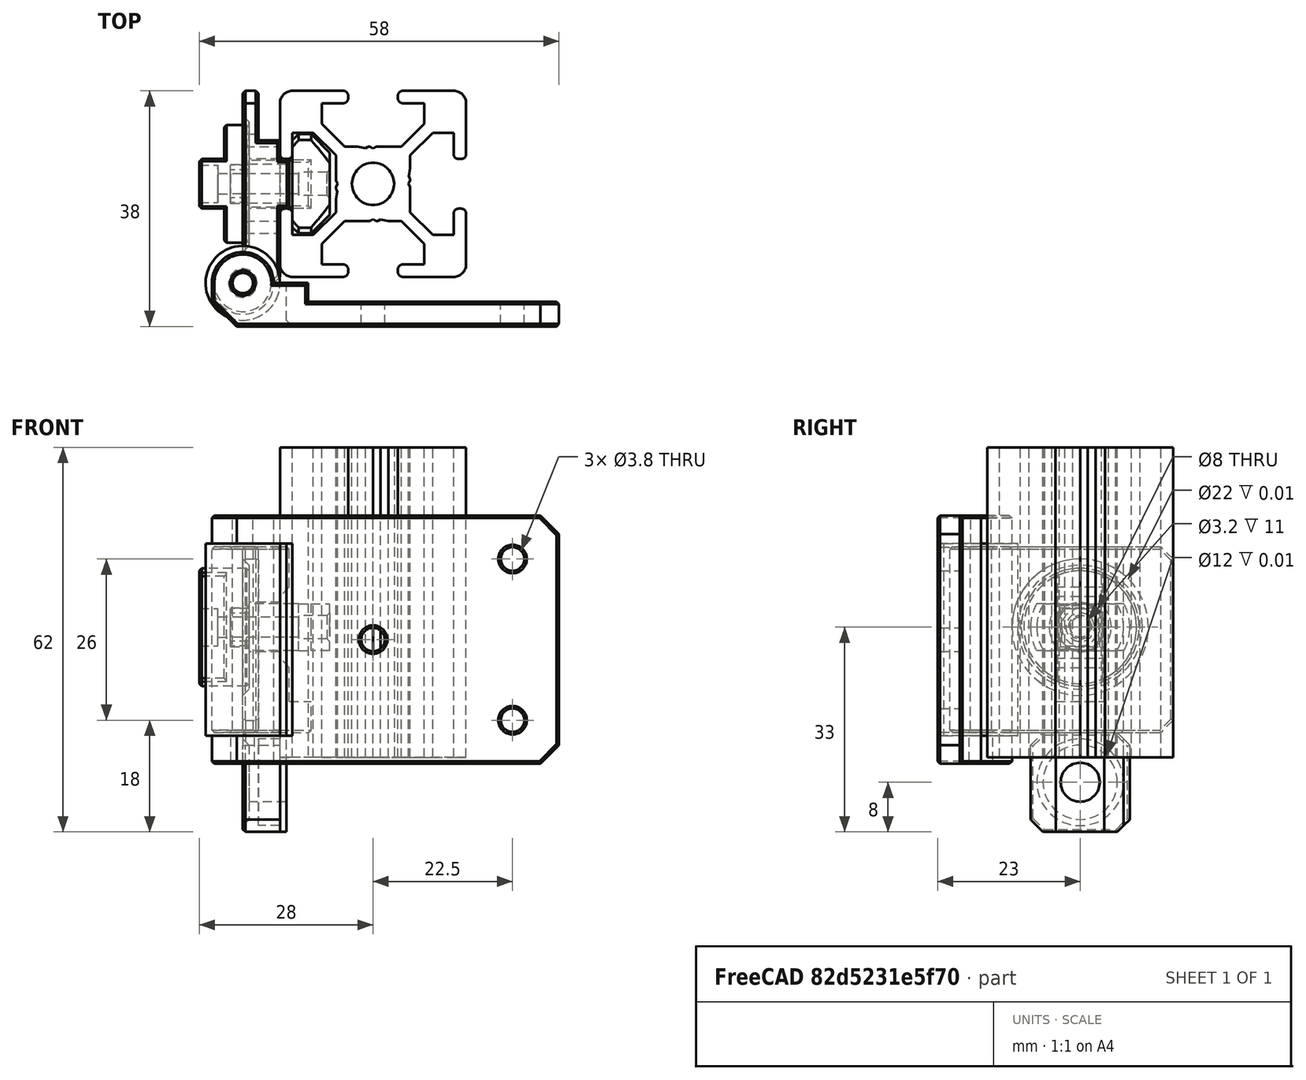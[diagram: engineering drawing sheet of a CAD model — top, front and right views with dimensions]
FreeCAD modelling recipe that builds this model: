
FCSTD DOCUMENT  (FreeCAD 0.19R24291 (Git))
Label: door-quick-release
License: Other
LicenseURL: GPL3
objects: Part::Cylinder×22, Part::Chamfer×18, Part::Box×16, Part::Cut×12, Part::MultiFuse×11, Part::Refine×3, Part::MultiCommon×3, Part::Feature×1, Part::Extrusion×1
note: 87 computed .brp shape members not serialized (recipe doc carries the construction recipe); baked Part::Feature solids carry a one-line shape summary decoded from their .brp

FEATURE [Part::Box] Box019  label="Cube018"
  AttacherType = Attacher::AttachEngine3D
  Height = 30
  Length = 6
  Placement = pos=(-6,0,0) rot=(0,0,1;0rad)
  Width = 30
FEATURE [Part::Box] Box020  label="Cube019"
  AttacherType = Attacher::AttachEngine3D
  Height = 12
  Length = 1.5
  Placement = pos=(0,11.1,0) rot=(0,0,1;0rad)
  Width = 7.8
FEATURE [Part::Cylinder] Cylinder
  Angle = 360
  AttacherType = Attacher::AttachEngine3D
  Height = 10
  Placement = pos=(3,15,17) rot=(0,-1,0;1.5708rad)
  Radius = 4
FEATURE [Part::Cylinder] Cylinder001
  Angle = 360
  AttacherType = Attacher::AttachEngine3D
  Height = 10
  Placement = pos=(-5,15,17) rot=(0,-1,0;1.5708rad)
  Radius = 11
FEATURE [Part::Cylinder] Cylinder002
  Angle = 360
  AttacherType = Attacher::AttachEngine3D
  Height = 30
  Placement = pos=(-6,-1,0) rot=(0,0,1;0rad)
  Radius = 5
FEATURE [Part::Box] Box  label="Cube"
  AttacherType = Attacher::AttachEngine3D
  Height = 30
  Length = 2
  Placement = pos=(-2,-1,0) rot=(0,0,1;0rad)
  Width = 2
FEATURE [Part::Chamfer] Chamfer006006002
  Base = -> Box
  Edges = 1 edges r=1: [Edge5]
FEATURE [Part::Cylinder] Cylinder003
  Angle = 360
  AttacherType = Attacher::AttachEngine3D
  Height = 30
  Placement = pos=(-6,-1,0) rot=(0,0,1;0rad)
  Radius = 1.7
FEATURE [Part::Box] Box021  label="Cube020"
  AttacherType = Attacher::AttachEngine3D
  Height = 5
  Length = 5
  Placement = pos=(0,11.1,0) rot=(0,0,1;0rad)
  Width = 7.8
FEATURE [Part::Box] Box022  label="Cube021"
  AttacherType = Attacher::AttachEngine3D
  Height = 8
  Length = 1.5
  Placement = pos=(0,11.1,22) rot=(0,0,1;0rad)
  Width = 7.8
FEATURE [Part::Chamfer] Chamfer
  Base = -> Box020
  Edges = 1 edges r=1.49: [Edge6]
FEATURE [Part::Chamfer] Chamfer006006003
  Base = -> Box022
  Edges = 1 edges r=1.49: [Edge8]
FEATURE [Part::Chamfer] Chamfer006006004
  Base = -> Box019
  Edges = 2 edges r=2: [Edge11,Edge12]
FEATURE [Part::Cut] Cut
  Base = -> Chamfer006006004
  Tool = -> Cylinder
FEATURE [Part::Cut] Cut001
  Base = -> Cut
  Tool = -> Cylinder001
FEATURE [Part::Chamfer] Chamfer006006005
  Base = -> Cut001
  Edges = 1 edges r=0.99: [Edge21]
FEATURE [Part::MultiFuse] Fusion
  Shapes = -> [Chamfer006006005,Chamfer006006003,Chamfer,Box021,Chamfer006006002,Cylinder002]
FEATURE [Part::Cut] Cut002
  Base = -> Fusion
  Tool = -> Cylinder003
FEATURE [Part::Refine] Cut002001
  Source = -> Cut002
FEATURE [Part::Cylinder] Cylinder004
  Angle = 360
  AttacherType = Attacher::AttachEngine3D
  Height = 40
  Placement = pos=(-6,-1,0) rot=(0,0,1;0rad)
  Radius = 5
FEATURE [Part::Box] Box023  label="Cube022"
  AttacherType = Attacher::AttachEngine3D
  Height = 40
  Length = 46
  Placement = pos=(4.5,-4,0) rot=(0,0,1;0rad)
  Width = 4
FEATURE [Part::Box] Box024  label="Cube023"
  AttacherType = Attacher::AttachEngine3D
  Height = 40
  Length = 56
  Placement = pos=(-11,-8,0) rot=(0,0,1;0rad)
  Width = 7
FEATURE [Part::Cylinder] Cylinder005
  Angle = 360
  AttacherType = Attacher::AttachEngine3D
  Height = 31
  Placement = pos=(-6,-1,4.5) rot=(0,0,1;0rad)
  Radius = 6
FEATURE [Part::Chamfer] Chamfer006006007
  Base = -> Box024
  Edges = 1 edges r=4: [Edge1]
FEATURE [Part::Cut] Cut002002
  Base = -> Chamfer006006007
  Tool = -> Box023
FEATURE [Part::Chamfer] Chamfer006006008
  Base = -> Cut002002
  Edges = 2 edges r=3: [Edge8,Edge16]
FEATURE [Part::MultiFuse] Fusion001
  Shapes = -> [Chamfer006006008,Cylinder004]
FEATURE [Part::Box] Box025  label="Cube024"
  AttacherType = Attacher::AttachEngine3D
  Height = 31
  Length = 13
  Placement = pos=(-12,-9,4.5) rot=(0,0,1;0rad)
  Width = 14
FEATURE [Part::Cut] Cut002003
  Base = -> Fusion001
  Tool = -> Box025
FEATURE [Part::Chamfer] Chamfer006006009
  Base = -> Cut002003
  Edges = 1 edges r=1: [Edge18]
FEATURE [Part::Cylinder] Cylinder006
  Angle = 360
  AttacherType = Attacher::AttachEngine3D
  Height = 10
  Placement = pos=(-6,-1,0) rot=(0,0,1;0rad)
  Radius = 1.9
FEATURE [Part::Cylinder] Cylinder007
  Angle = 360
  AttacherType = Attacher::AttachEngine3D
  Height = 10
  Placement = pos=(15,-9,20) rot=(-1,0,0;1.5708rad)
  Radius = 1.9
FEATURE [Part::Cylinder] Cylinder008
  Angle = 360
  AttacherType = Attacher::AttachEngine3D
  Height = 10
  Placement = pos=(37.5,-9,33) rot=(-1,0,0;1.5708rad)
  Radius = 1.9
FEATURE [Part::Cylinder] Cylinder009
  Angle = 360
  AttacherType = Attacher::AttachEngine3D
  Height = 10
  Placement = pos=(37.5,-9,7) rot=(-1,0,0;1.5708rad)
  Radius = 1.9
FEATURE [Part::MultiFuse] Fusion002
  Shapes = -> [Cylinder009,Cylinder008,Cylinder007]
FEATURE [Part::Cylinder] Cylinder010
  Angle = 360
  AttacherType = Attacher::AttachEngine3D
  Height = 10
  Placement = pos=(-6,-1,30) rot=(0,0,1;0rad)
  Radius = 1.65
FEATURE [Part::MultiFuse] Fusion003
  Shapes = -> [Cylinder010,Cylinder006]
FEATURE [Part::MultiFuse] Fusion004
  Shapes = -> [Fusion003,Fusion002]
FEATURE [Part::Cut] Cut002004
  Base = -> Chamfer006006009
  Tool = -> Fusion004
FEATURE [Part::Refine] Cut002004001
  Source = -> Cut002004
FEATURE [Part::Chamfer] Chamfer006006010
  Base = -> Cut002004001
  Edges = 27 edges r=0.4: [Edge5,Edge6,Edge8,Edge9,Edge10,Edge11,Edge12,Edge13,Edge23,Edge32,Edge34,Edge36,Edge39,Edge47,Edge49,Edge52,Edge54,Edge56,Edge57,Edge59,Edge60,Edge62,Edge63,Edge64,Edge65,Edge67,Edge68]
FEATURE [Part::Box] Box026  label="Cube025"
  AttacherType = Attacher::AttachEngine3D
  Height = 16
  Length = 6
  Placement = pos=(-6,7,0) rot=(0,0,1;0rad)
  Width = 16
FEATURE [Part::Box] Box027  label="Cube026"
  AttacherType = Attacher::AttachEngine3D
  Height = 16
  Length = 1
  Placement = pos=(0,11.1,0) rot=(0,0,1;0rad)
  Width = 7.8
FEATURE [Part::Cylinder] Cylinder011
  Angle = 360
  AttacherType = Attacher::AttachEngine3D
  Height = 10
  Placement = pos=(2,15,8) rot=(0,-1,0;1.5708rad)
  Radius = 3.15
FEATURE [Part::Cylinder] Cylinder012
  Angle = 360
  AttacherType = Attacher::AttachEngine3D
  Height = 10
  Placement = pos=(-5,15,8) rot=(0,-1,0;1.5708rad)
  Radius = 6
FEATURE [Part::MultiFuse] Fusion005
  Shapes = -> [Cylinder012,Cylinder011]
FEATURE [Part::MultiFuse] Fusion006
  Shapes = -> [Box027,Box026]
FEATURE [Part::Cut] Cut002004002
  Base = -> Fusion006
  Tool = -> Fusion005
FEATURE [Part::Chamfer] Chamfer006006011
  Base = -> Cut002004002
  Edges = 1 edges r=0.99: [Edge5]
FEATURE [Part::Chamfer] Chamfer006006012
  Base = -> Chamfer006006011
  Edges = 4 edges r=2: [Edge8,Edge10,Edge14,Edge18]
FEATURE [Part::Chamfer] Chamfer006006013
  Base = -> Chamfer006006012
  Edges = 8 edges r=0.4: [Edge1,Edge2,Edge3,Edge4,Edge5,Edge6,Edge7,Edge8]
  Placement = pos=(0,0,-11) rot=(0,0,1;0rad)
FEATURE [Part::Feature] Cut002004003_cs
  shape: bbox 30 x 30 x 4e-07 mm, 0 faces, 0 solids (baked)
FEATURE [Part::Extrusion] Extrude
  Base = -> Cut002004003_cs
  Dir = (0,0,1)
  DirMode = 2
  FaceMakerClass = Part::FaceMakerBullseye
  LengthFwd = 50
  LengthRev = 0
  Solid = true
  Symmetric = false
FEATURE [Part::Cylinder] Cylinder013
  Angle = 360
  AttacherType = Attacher::AttachEngine3D
  Height = 7.25
  Placement = pos=(2.25,15,22) rot=(0,-1,0;1.5708rad)
  Radius = 3.75
FEATURE [Part::Box] Box028  label="Cube027"
  AttacherType = Attacher::AttachEngine3D
  Height = 7.5
  Length = 6
  Placement = pos=(2,7,18.25) rot=(0,0,1;0rad)
  Width = 16
FEATURE [Part::Chamfer] Chamfer006006014
  Base = -> Box028
  Edges = 2 edges r=3: [Edge5,Edge7]
  Placement = pos=(0.25,0,0) rot=(0,0,1;0rad)
FEATURE [Part::Box] Box029  label="Cube028"
  AttacherType = Attacher::AttachEngine3D
  Height = 6
  Length = 3
  Placement = pos=(-8,12,19) rot=(0,0,1;0rad)
  Width = 6
FEATURE [Part::Cylinder] Cylinder014
  Angle = 360
  AttacherType = Attacher::AttachEngine3D
  Height = 7.25
  Placement = pos=(-3.75,15,22) rot=(0,-1,0;1.5708rad)
  Radius = 3.75
FEATURE [Part::MultiCommon] Common
  Shapes = -> [Cylinder014,Box029]
FEATURE [Part::Cylinder] Cylinder015
  Angle = 360
  AttacherType = Attacher::AttachEngine3D
  Height = 6
  Placement = pos=(2.25,15,22) rot=(0,1,0;1.5708rad)
  Radius = 8
FEATURE [Part::Cylinder] Cylinder016
  Angle = 360
  AttacherType = Attacher::AttachEngine3D
  Height = 30.25
  Placement = pos=(9.25,15,22) rot=(0,-1,0;1.5708rad)
  Radius = 1.6
FEATURE [Part::Cylinder] Cylinder017
  Angle = 360
  AttacherType = Attacher::AttachEngine3D
  Height = 5
  Placement = pos=(8.25,15,22) rot=(0,-1,0;1.5708rad)
  Radius = 1.9
FEATURE [Part::MultiFuse] Fusion008
  Placement = pos=(-0.25,0,0) rot=(0,0,1;0rad)
  Shapes = -> [Cylinder016,Cylinder017]
FEATURE [Part::Cylinder] Cylinder018
  Angle = 360
  AttacherType = Attacher::AttachEngine3D
  Height = 10
  Placement = pos=(-5,15,22) rot=(0,-1,0;1.5708rad)
  Radius = 9.5
FEATURE [Part::Box] Box030  label="Cube029"
  AttacherType = Attacher::AttachEngine3D
  Height = 20
  Length = 4
  Placement = pos=(-13,11,12) rot=(0,0,1;0rad)
  Width = 8
FEATURE [Part::Cylinder] Cylinder019
  Angle = 360
  AttacherType = Attacher::AttachEngine3D
  Height = 4
  Placement = pos=(-5,15,22) rot=(0,-1,0;1.5708rad)
  Radius = 9.5
FEATURE [Part::MultiCommon] Common002
  Shapes = -> [Cylinder018,Box030]
FEATURE [Part::MultiFuse] Fusion009
  Shapes = -> [Cylinder019,Common002]
FEATURE [Part::Cylinder] Cylinder020
  Angle = 360
  AttacherType = Attacher::AttachEngine3D
  Height = 3
  Placement = pos=(-13,15,22) rot=(0,1,0;1.5708rad)
  Radius = 3
FEATURE [Part::Cylinder] Cylinder021
  Angle = 360
  AttacherType = Attacher::AttachEngine3D
  Height = 23
  Placement = pos=(-13,15,22) rot=(0,1,0;1.5708rad)
  Radius = 1.65
FEATURE [Part::MultiFuse] Fusion010
  Shapes = -> [Cylinder021,Cylinder020]
FEATURE [Part::Cut] Cut002004004
  Base = -> Fusion009
  Tool = -> Fusion010
FEATURE [Part::Box] Box031  label="Cube030"
  AttacherType = Attacher::AttachEngine3D
  Height = 6.3
  Length = 3
  Placement = pos=(-8,11.85,18.85) rot=(0,0,1;0rad)
  Width = 6.3
FEATURE [Part::Cut] Cut002004005
  Base = -> Cut002004004
  Tool = -> Box031
FEATURE [Part::Refine] Cut002004005001
  Source = -> Cut002004005
FEATURE [Part::Chamfer] Chamfer006006016
  Base = -> Cut002004005001
  Edges = 16 edges r=0.4: [Edge1,Edge3,Edge4,Edge5,Edge7,Edge8,Edge9,Edge10,Edge11,Edge12,Edge13,Edge18,Edge19,Edge20,Edge21,Edge22]
FEATURE [Part::Chamfer] Chamfer006006017
  Base = -> Cylinder015
  Edges = 1 edges r=3: [Edge1]
FEATURE [Part::MultiCommon] Common003
  Placement = pos=(-0.25,0,0) rot=(0,0,1;0rad)
  Shapes = -> [Chamfer006006017,Chamfer006006014]
FEATURE [Part::MultiFuse] Fusion011
  Shapes = -> [Common,Cylinder013,Common003]
FEATURE [Part::Cut] Cut002004005002
  Base = -> Fusion011
  Tool = -> Fusion008
FEATURE [Part::Chamfer] Chamfer006006018
  Base = -> Cut002004005002
  Edges = 1 edges r=0.4: [Edge66]
FEATURE [Part::Box] Box032  label="Cube031"
  AttacherType = Attacher::AttachEngine3D
  Height = 30
  Length = 10
  Placement = pos=(-3.5,22,0) rot=(0,0,1;0rad)
  Width = 10
FEATURE [Part::Cut] Cut002004005003
  Base = -> Cut002001
  Tool = -> Box032
FEATURE [Part::Chamfer] Chamfer006006019
  Base = -> Cut002004005003
  Edges = 32 edges r=0.4: [Edge1,Edge3,Edge5,Edge6,Edge7,Edge9,Edge10,Edge11,Edge12,Edge13,Edge14,Edge15,Edge16,Edge17,Edge18,Edge22,Edge28,Edge30,Edge31,Edge32,Edge33,Edge34,Edge35,Edge36,Edge37,Edge38,Edge42,Edge43,Edge44,Edge45,Edge47,Edge48]
  Placement = pos=(0,0,5) rot=(0,0,1;0rad)
FEATURE [Part::Chamfer] Chamfer006006020
  Base = -> Chamfer006006018
  Edges = 4 edges r=1: [Edge33,Edge35,Edge36,Edge37]
FEATURE [Part::Box] Box033  label="Cube032"
  AttacherType = Attacher::AttachEngine3D
  Height = 18
  Length = 10
  Placement = pos=(-3.5,22,-12.5) rot=(0,0,1;0rad)
  Width = 10
FEATURE [Part::Cut] Cut002004005004
  Base = -> Chamfer006006013
  Tool = -> Box033
